# Revit family: Safety & Protection_Barrier_UltiGroup_Column Tower Protector
name_source: partatom
category: Generic Models
revit_build: Autodesk Revit Architecture 2016 (Build: 20150220_1215(x64)
units: mm (PartAtom-declared; Revit-internal decimal feet)

## family parameters
Always vertical = Yes
Can host rebar = No
Cut with Voids When Loaded = No
OmniClass Number = 23.30.80.17.17
OmniClass Title = Column Protectors
Part Type = Normal
Room Calculation Point = No
Round Connector Dimension = Use Diameter
Shared = No
Work Plane-Based = No

## types (3) — shared parameters
Base Plate = Base Plate
Bolts = Bolts
Fax = 07 846 2467
Manufacturer = UltiGroup
Model = Ulti Impactable Column Tower Protector
PVC Black = PVC Black
PVC Yellow = PVC Yellow
Send Message = http://ultigroup.co.nz
Tower Post Height = 1150 mm
URL = www.ultigroup.co.nz
zero-valued in all types: InstallationGroup_ANZRS, ModifiedIssue_ANZRS

## per-type parameters (varying)
| type | Column Tower Protector Size | Description |
| 500mm x 500mm | 500 mm | Impactable PVC Column Tower Protector 500 x 500 |
| 600mm x 600mm | 600 mm | Impactable PVC Column Tower Protector 600 x 600 |
| 700mm x 700mm | 700 mm | Impactable PVC Column Tower Protector 700 x 700 |

## geometry (parser evidence)
native form markers: Blend x2, Sweep x3
no freeform markers — native parametric forms only
